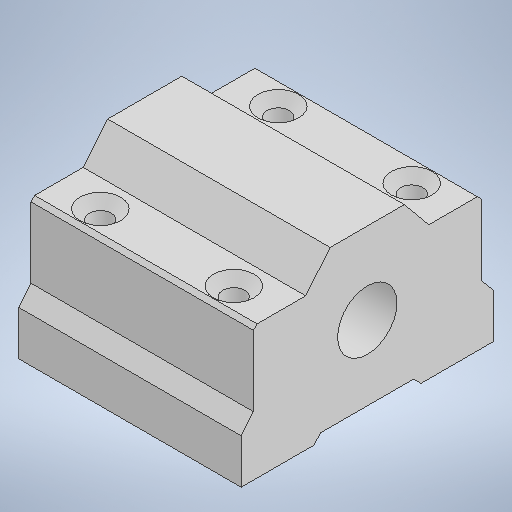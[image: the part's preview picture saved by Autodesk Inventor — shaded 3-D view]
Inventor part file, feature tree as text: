
AUTODESK INVENTOR PART (.ipt)
format: ipt  version: 2025.2 (Build 292293000, 293)  size: 237,056 bytes
history: native  units: mm
features: sketch x3, hole x2, extrude x1, chamfer x1
ambient origin geometry x8: Origin, YZ Plane, XZ Plane, XY Plane, X Axis, Y Axis, Z Axis, Center Point
bodies: Solid1 (feature_tree)
feature tree (7):
  extrude  "Extrusion1"  Depth=22.0mm
  hole  "Hole1"  [1 undecoded]
  hole  "Hole2"  [1 undecoded]
  chamfer  "Chamfer1"  Distance=8.0mm
  sketch  "Sketch1"  dims[d2=45.0deg d3=22.0mm]
  sketch  "Sketch2"  dims[d4=34.0mm d5=6.0mm]
  sketch  "Sketch3"  dims[d6=8.0mm d7=11.0mm d8=8.0mm d9=18.0mm d10=16.6mm d11=12.5mm d12=1.0mm d13=10.0mm d14=30.0mm d15=0.0mm d16=24.0mm d17=18.0mm d18=3.0mm d19=6.0mm d20=5.5mm d21=2.0mm d22=90.0deg d23=8.0mm d24=0.0mm d25=3.0mm d26=6.0mm d27=5.5mm d28=2.0mm d29=90.0deg d30=8.0mm d31=0.0mm d32=0.5mm d33=2.0mm d34=45.0deg]
note: 2 required parameter values undecoded (feature->parameter linkage not recoverable at this tier; creation-order binding heuristic only, values carry confidence <= 0.55)
